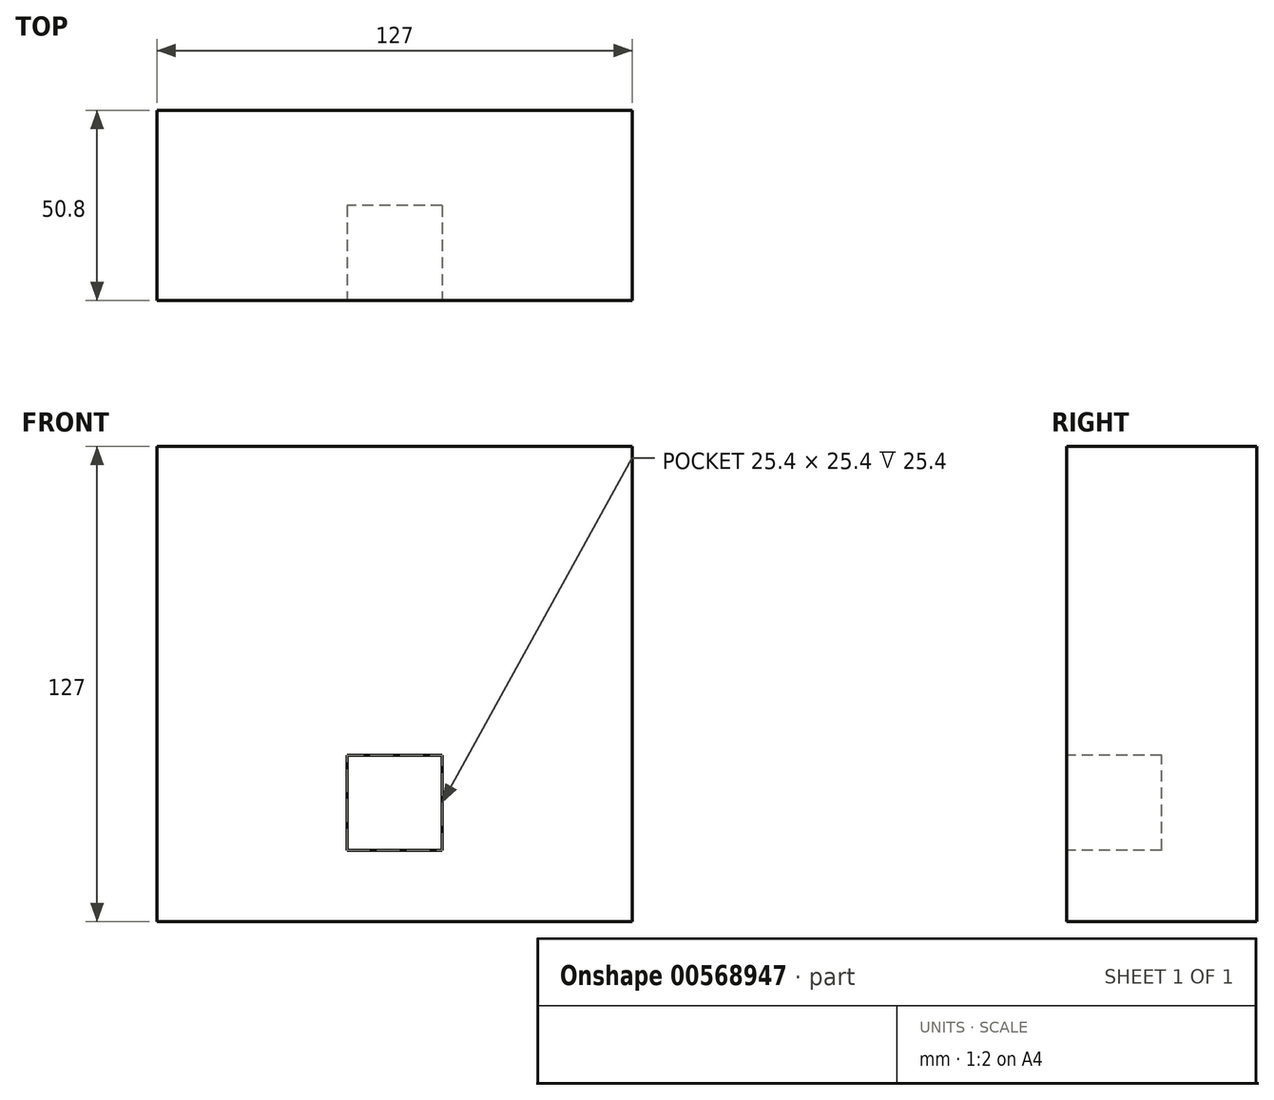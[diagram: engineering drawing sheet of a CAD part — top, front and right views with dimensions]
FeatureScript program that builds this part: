
annotation { "Feature Type Name" : "Feature", "Feature Type Description" : "" }
export const myFeature = defineFeature(function(context is Context, id is Id, definition is map)
    precondition{}
    {
        {
            var Q0;
            Q0=qCreatedBy(makeId("Front.planeOp"),FACE);
            var sketch = newSketch(context, id + "F0", { "sketchPlane" : qUnion([Q0])});
            skLineSegment(sketch, "E0.bottom", {"start": v(63.5, 63.5) * mm, "end": v(-63.5, 63.5) * mm});
            skLineSegment(sketch, "E0.top", {"start": v(63.5, -63.5) * mm, "end": v(-63.5, -63.5) * mm});
            skLineSegment(sketch, "E0.left", {"start": v(63.5, 63.5) * mm, "end": v(63.5, -63.5) * mm});
            skLineSegment(sketch, "E0.right", {"start": v(-63.5, 63.5) * mm, "end": v(-63.5, -63.5) * mm});
            skPoint(sketch, "E0.middle", {"position": v(0, 0) * mm});
            skPoint(sketch, "E1.middle", {"position": v(0, -31.75) * mm});
            skSolve(sketch);
        }
        {
            var Q0;
            Q0 = qSketchRegion(id + "F0", true);
            extrude(context, id + "F1", {"entities" : qUnion([Q0]), "depth" : 50.8 * mm, "offsetDistance" : 25.4 * mm});
        }
        {
            var Q0;
            Q0=makeQuery(id+"F1.opExtrude","CAP_FACE",FACE,{"disambiguationData":[OSD([sQuery(id+"F0.wireOp",EDGE,"E0.bottom"),sQuery(id+"F0.wireOp",EDGE,"E0.top"),sQuery(id+"F0.wireOp",EDGE,"E0.left"),sQuery(id+"F0.wireOp",EDGE,"E0.right")])],"isStart":false});
            var sketch = newSketch(context, id + "F2", { "sketchPlane" : qUnion([Q0])});
            skLineSegment(sketch, "E2.bottom", {"start": v(12.7, -44.45) * mm, "end": v(-12.7, -44.45) * mm});
            skLineSegment(sketch, "E2.top", {"start": v(12.7, -19.05) * mm, "end": v(-12.7, -19.05) * mm});
            skLineSegment(sketch, "E2.left", {"start": v(12.7, -44.45) * mm, "end": v(12.7, -19.05) * mm});
            skLineSegment(sketch, "E2.right", {"start": v(-12.7, -44.45) * mm, "end": v(-12.7, -19.05) * mm});
            skPoint(sketch, "E2.middle", {"position": v(0, -31.75) * mm});
            skSolve(sketch);
        }
        {
            var Q0;
            Q0 = qSketchRegion(id + "F2", true);
            extrude(context, id + "F3", {"entities" : qUnion([Q0]), "operationType" : NewBodyOperationType.REMOVE, "oppositeDirection" : true, "depth" : 25.4 * mm, "offsetDistance" : 25.4 * mm});
        }
    });
